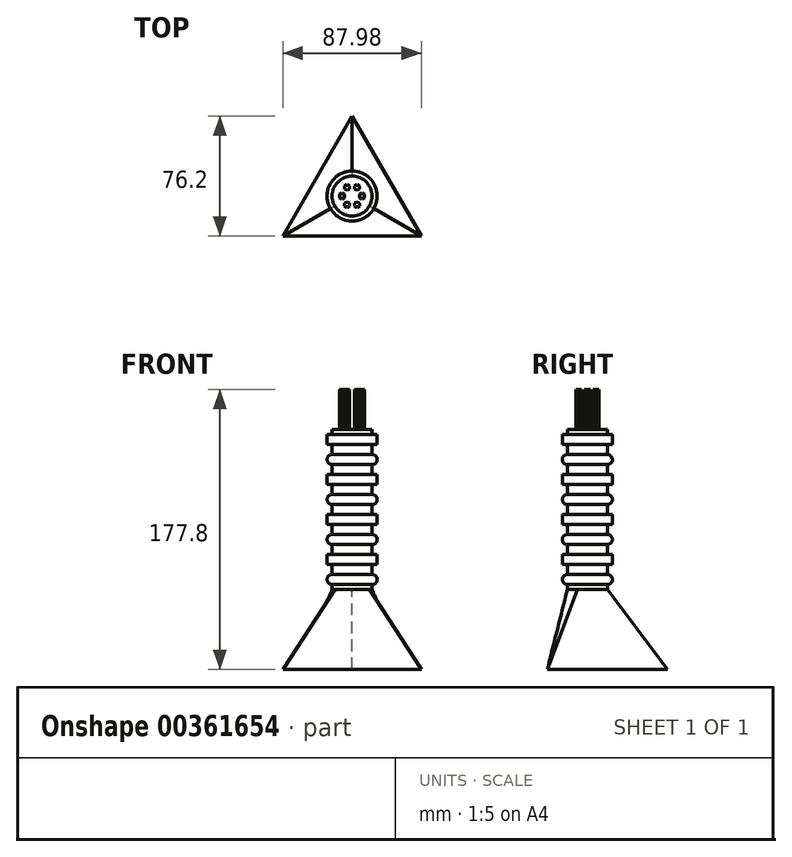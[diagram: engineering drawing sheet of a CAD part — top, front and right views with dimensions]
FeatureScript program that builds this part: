
annotation { "Feature Type Name" : "Feature", "Feature Type Description" : "" }
export const myFeature = defineFeature(function(context is Context, id is Id, definition is map)
    precondition{}
    {
        {
            var Q0;
            Q0=qCreatedBy(makeId("Front.planeOp"),FACE);
            var sketch = newSketch(context, id + "F0", { "sketchPlane" : qUnion([Q0])});
            skPoint(sketch, "E0.middle", {"position": v(0, 0) * mm});
            skLineSegment(sketch, "E1", {"start": v(12.7, 50.8) * mm, "end": v(12.7, 47.62) * mm});
            skLineSegment(sketch, "E2", {"start": v(12.7, 47.62) * mm, "end": v(15.87, 47.62) * mm});
            skLineSegment(sketch, "E3", {"start": v(15.87, 47.62) * mm, "end": v(15.87, 41.27) * mm});
            skLineSegment(sketch, "E4", {"start": v(15.87, 41.27) * mm, "end": v(12.7, 41.27) * mm});
            skLineSegment(sketch, "E5", {"start": v(12.7, 41.27) * mm, "end": v(12.7, 34.92) * mm});
            skArc(sketch, "E6", {"start": v(12.7, 28.57) * mm, "mid": v(15.88, 31.75) * mm, "end": v(12.7, 34.92) * mm});
            skLineSegment(sketch, "E7", {"start": v(12.7, 28.57) * mm, "end": v(12.7, 25.4) * mm});
            skLineSegment(sketch, "E8", {"start": v(12.7, 47.62) * mm, "end": v(12.7, 41.27) * mm, "construction": true});
            skLineSegment(sketch, "E9", {"start": v(12.7, 34.92) * mm, "end": v(12.7, 28.57) * mm, "construction": true});
            skLineSegment(sketch, "E10.direction2", {"start": v(0, 0) * mm, "end": v(0, 0) * mm});
            skLineSegment(sketch, "E11", {"start": v(12.7, 50.8) * mm, "end": v(0, 50.8) * mm});
            skLineSegment(sketch, "E12", {"start": v(0, 50.8) * mm, "end": v(0, -50.8) * mm});
            skLineSegment(sketch, "E13", {"start": v(0, -50.8) * mm, "end": v(12.7, -50.8) * mm});
            skLineSegment(sketch, "E14.0.1.0", {"start": v(12.7, 25.4) * mm, "end": v(12.7, 22.22) * mm});
            skLineSegment(sketch, "E14.0.1.1", {"start": v(12.7, 22.23) * mm, "end": v(15.87, 22.23) * mm});
            skLineSegment(sketch, "E14.0.1.2", {"start": v(15.87, 22.23) * mm, "end": v(15.87, 15.88) * mm});
            skLineSegment(sketch, "E14.0.1.3", {"start": v(15.87, 15.87) * mm, "end": v(12.7, 15.87) * mm});
            skLineSegment(sketch, "E14.0.1.4", {"start": v(12.7, 15.87) * mm, "end": v(12.7, 9.52) * mm});
            skArc(sketch, "E14.0.1.5", {"start": v(12.7, 3.17) * mm, "mid": v(15.88, 6.35) * mm, "end": v(12.7, 9.52) * mm});
            skLineSegment(sketch, "E14.0.1.6", {"start": v(12.7, 3.17) * mm, "end": v(12.7, 0) * mm});
            skLineSegment(sketch, "E14.0.2.0", {"start": v(12.7, 0) * mm, "end": v(12.7, -3.17) * mm});
            skLineSegment(sketch, "E14.0.2.1", {"start": v(12.7, -3.17) * mm, "end": v(15.87, -3.17) * mm});
            skLineSegment(sketch, "E14.0.2.2", {"start": v(15.87, -3.17) * mm, "end": v(15.87, -9.52) * mm});
            skLineSegment(sketch, "E14.0.2.3", {"start": v(15.87, -9.53) * mm, "end": v(12.7, -9.53) * mm});
            skLineSegment(sketch, "E14.0.2.4", {"start": v(12.7, -9.53) * mm, "end": v(12.7, -15.88) * mm});
            skArc(sketch, "E14.0.2.5", {"start": v(12.7, -22.23) * mm, "mid": v(15.88, -19.05) * mm, "end": v(12.7, -15.88) * mm});
            skLineSegment(sketch, "E14.0.2.6", {"start": v(12.7, -22.23) * mm, "end": v(12.7, -25.4) * mm});
            skLineSegment(sketch, "E14.0.3.0", {"start": v(12.7, -25.4) * mm, "end": v(12.7, -28.57) * mm});
            skLineSegment(sketch, "E14.0.3.1", {"start": v(12.7, -28.57) * mm, "end": v(15.87, -28.57) * mm});
            skLineSegment(sketch, "E14.0.3.2", {"start": v(15.87, -28.57) * mm, "end": v(15.87, -34.92) * mm});
            skLineSegment(sketch, "E14.0.3.3", {"start": v(15.87, -34.93) * mm, "end": v(12.7, -34.93) * mm});
            skLineSegment(sketch, "E14.0.3.4", {"start": v(12.7, -34.92) * mm, "end": v(12.7, -41.28) * mm});
            skArc(sketch, "E14.0.3.5", {"start": v(12.7, -47.63) * mm, "mid": v(15.88, -44.45) * mm, "end": v(12.7, -41.28) * mm});
            skLineSegment(sketch, "E14.0.3.6", {"start": v(12.7, -47.62) * mm, "end": v(12.7, -50.8) * mm});
            skLineSegment(sketch, "E14.direction1", {"start": v(12.7, 25.4) * mm, "end": v(38.1, 25.4) * mm, "construction": true});
            skLineSegment(sketch, "E14.direction2", {"start": v(12.7, 25.4) * mm, "end": v(12.7, 0) * mm, "construction": true});
            skSolve(sketch);
        }
        {
            var Q0;
            Q0=qCreatedBy(makeId("Top.planeOp"),FACE);
            cPlane(context, id + "F1", {"entities" : qUnion([Q0]), "cplaneType" : CPlaneType.OFFSET, "offset" : 101.6 * mm, "oppositeDirection" : true, "width" : 152.4 * mm, "height" : 152.4 * mm});
        }
        {
            var Q0;
            Q0=qCreatedBy(id+"F1.planeOp",FACE);
            var sketch = newSketch(context, id + "F2", { "sketchPlane" : qUnion([Q0])});
            skCircle(sketch, "E15.cCircle", {"center": v(0, 0) * mm, "radius": 25.4 * mm, "construction": true});
            skLineSegment(sketch, "E15.0", {"start": v(44, -25.4) * mm, "end": v(-44, -25.4) * mm});
            skLineSegment(sketch, "E15.1", {"start": v(-44, -25.4) * mm, "end": v(0, 50.8) * mm});
            skLineSegment(sketch, "E15.2", {"start": v(0, 50.8) * mm, "end": v(44, -25.4) * mm});
            skPoint(sketch, "E15.0.midPoint", {"position": v(0, -25.4) * mm});
            skSolve(sketch);
        }
        {
            var Q0;
            Q0=qCreatedBy(makeId("Top.planeOp"),FACE);
            cPlane(context, id + "F3", {"entities" : qUnion([Q0]), "cplaneType" : CPlaneType.OFFSET, "offset" : 50.8 * mm, "width" : 152.4 * mm, "height" : 152.4 * mm});
        }
        {
            var Q0;
            Q0=qCreatedBy(id+"F3.planeOp",FACE);
            var sketch = newSketch(context, id + "F4", { "sketchPlane" : qUnion([Q0])});
            skCircle(sketch, "E16", {"center": v(0, 0) * mm, "radius": 6.35 * mm, "construction": true});
            skCircle(sketch, "E17.cCircle", {"center": v(-6.35, 0) * mm, "radius": 1.59 * mm, "construction": true});
            skLineSegment(sketch, "E17.0", {"start": v(-4.76, 0.92) * mm, "end": v(-4.76, -0.92) * mm});
            skLineSegment(sketch, "E17.1", {"start": v(-4.76, -0.92) * mm, "end": v(-6.35, -1.83) * mm});
            skLineSegment(sketch, "E17.2", {"start": v(-6.35, -1.83) * mm, "end": v(-7.94, -0.92) * mm});
            skLineSegment(sketch, "E17.3", {"start": v(-7.94, -0.92) * mm, "end": v(-7.94, 0.92) * mm});
            skLineSegment(sketch, "E17.4", {"start": v(-7.94, 0.92) * mm, "end": v(-6.35, 1.83) * mm});
            skLineSegment(sketch, "E17.5", {"start": v(-6.35, 1.83) * mm, "end": v(-4.76, 0.92) * mm});
            skPoint(sketch, "E17.0.midPoint", {"position": v(-4.76, 0) * mm});
            skLineSegment(sketch, "E18.1.0", {"start": v(-1.59, -4.58) * mm, "end": v(-1.59, -6.42) * mm});
            skLineSegment(sketch, "E18.1.1", {"start": v(-3.18, -3.67) * mm, "end": v(-1.59, -4.58) * mm});
            skCircle(sketch, "E18.1.2", {"center": v(-3.18, -5.5) * mm, "radius": 1.59 * mm, "construction": true});
            skLineSegment(sketch, "E18.1.3", {"start": v(-4.76, -4.58) * mm, "end": v(-3.17, -3.67) * mm});
            skLineSegment(sketch, "E18.1.4", {"start": v(-3.18, -7.33) * mm, "end": v(-4.76, -6.42) * mm});
            skLineSegment(sketch, "E18.1.5", {"start": v(-4.76, -6.42) * mm, "end": v(-4.76, -4.58) * mm});
            skPoint(sketch, "E18.1.6", {"position": v(-2.38, -4.12) * mm});
            skLineSegment(sketch, "E18.2.0", {"start": v(3.17, -3.67) * mm, "end": v(4.76, -4.58) * mm});
            skLineSegment(sketch, "E18.2.1", {"start": v(1.59, -4.58) * mm, "end": v(3.17, -3.67) * mm});
            skCircle(sketch, "E18.2.2", {"center": v(3.17, -5.5) * mm, "radius": 1.59 * mm, "construction": true});
            skLineSegment(sketch, "E18.2.3", {"start": v(1.59, -6.42) * mm, "end": v(1.59, -4.58) * mm});
            skLineSegment(sketch, "E18.2.4", {"start": v(4.76, -6.42) * mm, "end": v(3.17, -7.33) * mm});
            skLineSegment(sketch, "E18.2.5", {"start": v(3.17, -7.33) * mm, "end": v(1.59, -6.42) * mm});
            skPoint(sketch, "E18.2.6", {"position": v(2.38, -4.12) * mm});
            skLineSegment(sketch, "E18.3.0", {"start": v(4.76, 0.92) * mm, "end": v(6.35, 1.83) * mm});
            skLineSegment(sketch, "E18.3.1", {"start": v(4.76, -0.92) * mm, "end": v(4.76, 0.92) * mm});
            skCircle(sketch, "E18.3.2", {"center": v(6.35, 0) * mm, "radius": 1.59 * mm, "construction": true});
            skLineSegment(sketch, "E18.3.3", {"start": v(6.35, -1.83) * mm, "end": v(4.76, -0.92) * mm});
            skLineSegment(sketch, "E18.3.4", {"start": v(7.94, 0.92) * mm, "end": v(7.94, -0.92) * mm});
            skLineSegment(sketch, "E18.3.5", {"start": v(7.94, -0.92) * mm, "end": v(6.35, -1.83) * mm});
            skPoint(sketch, "E18.3.6", {"position": v(4.76, 0) * mm});
            skLineSegment(sketch, "E18.4.0", {"start": v(1.59, 4.58) * mm, "end": v(1.59, 6.42) * mm});
            skLineSegment(sketch, "E18.4.1", {"start": v(3.18, 3.67) * mm, "end": v(1.59, 4.58) * mm});
            skLineSegment(sketch, "E18.4.3", {"start": v(4.76, 4.58) * mm, "end": v(3.18, 3.67) * mm});
            skLineSegment(sketch, "E18.4.4", {"start": v(3.18, 7.33) * mm, "end": v(4.76, 6.42) * mm});
            skLineSegment(sketch, "E18.4.5", {"start": v(4.76, 6.42) * mm, "end": v(4.76, 4.58) * mm});
            skPoint(sketch, "E18.4.6", {"position": v(2.38, 4.12) * mm});
            skLineSegment(sketch, "E18.5.0", {"start": v(-3.17, 3.67) * mm, "end": v(-4.76, 4.58) * mm});
            skLineSegment(sketch, "E18.5.1", {"start": v(-1.59, 4.58) * mm, "end": v(-3.18, 3.67) * mm});
            skLineSegment(sketch, "E18.5.3", {"start": v(-1.59, 6.42) * mm, "end": v(-1.59, 4.58) * mm});
            skLineSegment(sketch, "E18.5.4", {"start": v(-4.76, 6.42) * mm, "end": v(-3.18, 7.33) * mm});
            skLineSegment(sketch, "E18.5.5", {"start": v(-3.18, 7.33) * mm, "end": v(-1.59, 6.42) * mm});
            skPoint(sketch, "E18.5.6", {"position": v(-2.38, 4.12) * mm});
            skSolve(sketch);
        }
        {
            var Q0;
            Q0=makeQuery(id+"F0.imprint","IMPRINT",FACE,{"disambiguationData":[TD([[makeQuery(id+"F0.imprint","IMPRINT",EDGE,{"derivedFrom":sQuery(id+"F0.wireOp",EDGE,"E1")}),-1.0]])]});
            var Q1;
            Q1=sQuery(id+"F0.wireOp",EDGE,"E12");
            revolve(context, id + "F5", {"entities" : qUnion([Q0]), "axis" : qUnion([Q1]), "revolveType" : RevolveType.FULL});
        }
        {
            var Q0;
            Q0=makeQuery(id+"F2.imprint","IMPRINT",FACE,{"disambiguationData":[TD([[makeQuery(id+"F2.imprint","IMPRINT",EDGE,{"derivedFrom":sQuery(id+"F2.wireOp",EDGE,"E15.0")}),-1.0]])]});
            var Q1;
            Q1=makeQuery(id+"F5.opRevolve","SWEPT_FACE",FACE,{"disambiguationData":[OSD([sQuery(id+"F0.wireOp",EDGE,"E13")])]});
            loft(context, id + "F6", {"operationType" : NewBodyOperationType.ADD, "sheetProfilesArray" : [{ "sheetProfileEntities" : qUnion([Q0]) }, { "sheetProfileEntities" : qUnion([Q1]) }]});
        }
        {
            var Q0;
            Q0 = qSketchRegion(id + "F4", true);
            extrude(context, id + "F7", {"entities" : qUnion([Q0]), "depth" : 25.4 * mm});
        }
        {
            var Q0;
            Q0=makeQuery(id+"F7.opExtrude","SWEPT_BODY",BODY,{"disambiguationData":[OSD([sQuery(id+"F4.wireOp",EDGE,"E17.0"),sQuery(id+"F4.wireOp",EDGE,"E17.1"),sQuery(id+"F4.wireOp",EDGE,"E17.2"),sQuery(id+"F4.wireOp",EDGE,"E17.3"),sQuery(id+"F4.wireOp",EDGE,"E17.4"),sQuery(id+"F4.wireOp",EDGE,"E17.5")])]});
            var Q1;
            Q1=makeQuery(id+"F5.opRevolve","SWEPT_EDGE",EDGE,{"disambiguationData":[OSD([sQuery(id+"F0.wireOp",EDGE,"E1"),sQuery(id+"F0.wireOp",EDGE,"E11")])]});
            circularPattern(context, id + "F8", {"operationType" : NewBodyOperationType.ADD, "entities" : qUnion([Q0]), "axis" : qUnion([Q1]), "angle" : 360 * degree, "instanceCount" : 6, "equalSpace" : true});
        }
    });
